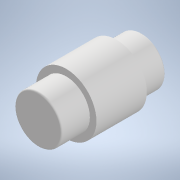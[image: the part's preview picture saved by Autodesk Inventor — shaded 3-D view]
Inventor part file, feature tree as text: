
AUTODESK INVENTOR PART (.ipt)
format: ipt  version: 2020.3 (Build 243373000, 373)  size: 128,000 bytes
history: native  units: mm
features: extrude x3, sketch x3, fillet x1
ambient origin geometry x8: Origin, YZ Plane, XZ Plane, XY Plane, X Axis, Y Axis, Z Axis, Center Point
bodies: Solid1 (feature_tree)
feature tree (7):
  extrude  "Extrusion1"  Depth=5.0mm TaperAngle=0.0deg
  extrude  "Extrusion2"  Depth=10.0mm TaperAngle=0.0deg
  extrude  "Extrusion3"  Depth=5.556mm TaperAngle=0.0deg
  fillet  "Fillet1"  Radius=0.3mm
  sketch  "Sketch1"  dims[d0=9.4mm d1=5.0mm d2=0.0mm]
  sketch  "Sketch2"  dims[d3=12.0mm d4=10.0mm d5=0.0mm]
  sketch  "Sketch3"  dims[d6=9.4mm d7=5.556mm d8=0.0mm d9=0.3mm]
